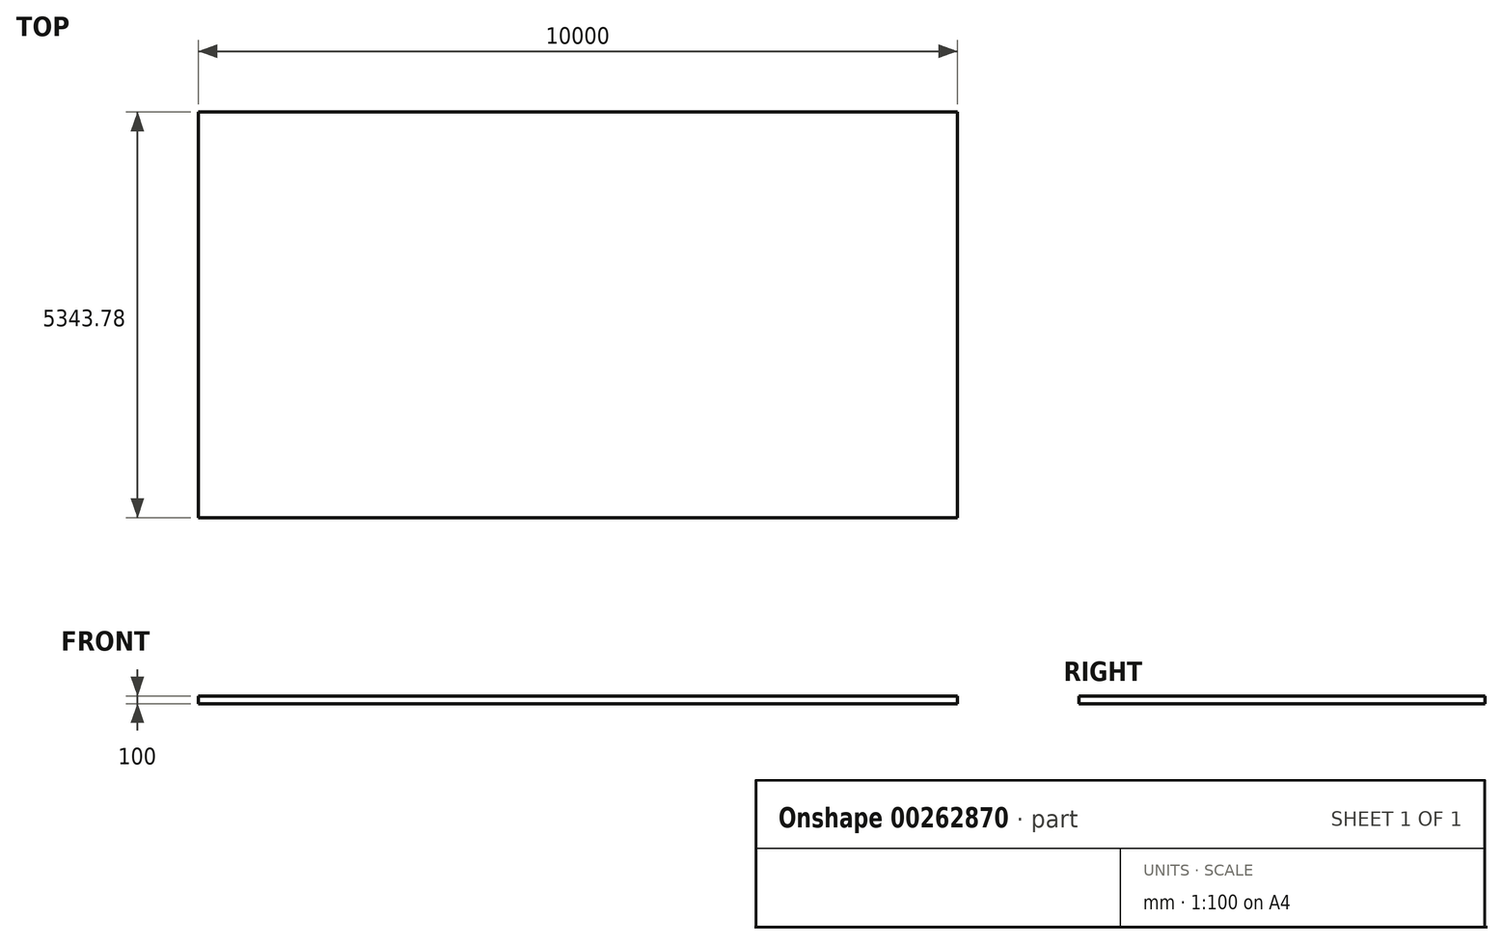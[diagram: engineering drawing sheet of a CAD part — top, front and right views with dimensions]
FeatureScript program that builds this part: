
annotation { "Feature Type Name" : "Feature", "Feature Type Description" : "" }
export const myFeature = defineFeature(function(context is Context, id is Id, definition is map)
    precondition{}
    {
        {
            var Q0;
            Q0=qCreatedBy(makeId("Top.planeOp"),FACE);
            var sketch = newSketch(context, id + "F0", { "sketchPlane" : qUnion([Q0])});
            skLineSegment(sketch, "E0.bottom", {"start": v(5000, -2671.9) * mm, "end": v(-5000, -2671.9) * mm});
            skLineSegment(sketch, "E0.top", {"start": v(5000, 2671.9) * mm, "end": v(-5000, 2671.9) * mm});
            skLineSegment(sketch, "E0.left", {"start": v(5000, -2671.9) * mm, "end": v(5000, 2671.9) * mm});
            skLineSegment(sketch, "E0.right", {"start": v(-5000, -2671.9) * mm, "end": v(-5000, 2671.9) * mm});
            skPoint(sketch, "E0.middle", {"position": v(0, 0) * mm});
            skSolve(sketch);
        }
        {
            var Q0;
            Q0=makeQuery(id+"F0.imprint","IMPRINT",FACE,{"disambiguationData":[TD([[makeQuery(id+"F0.imprint","IMPRINT",EDGE,{"derivedFrom":sQuery(id+"F0.wireOp",EDGE,"E0.bottom")}),-1.0]])]});
            extrude(context, id + "F1", {"entities" : qUnion([Q0]), "depth" : 100 * mm});
        }
    });
